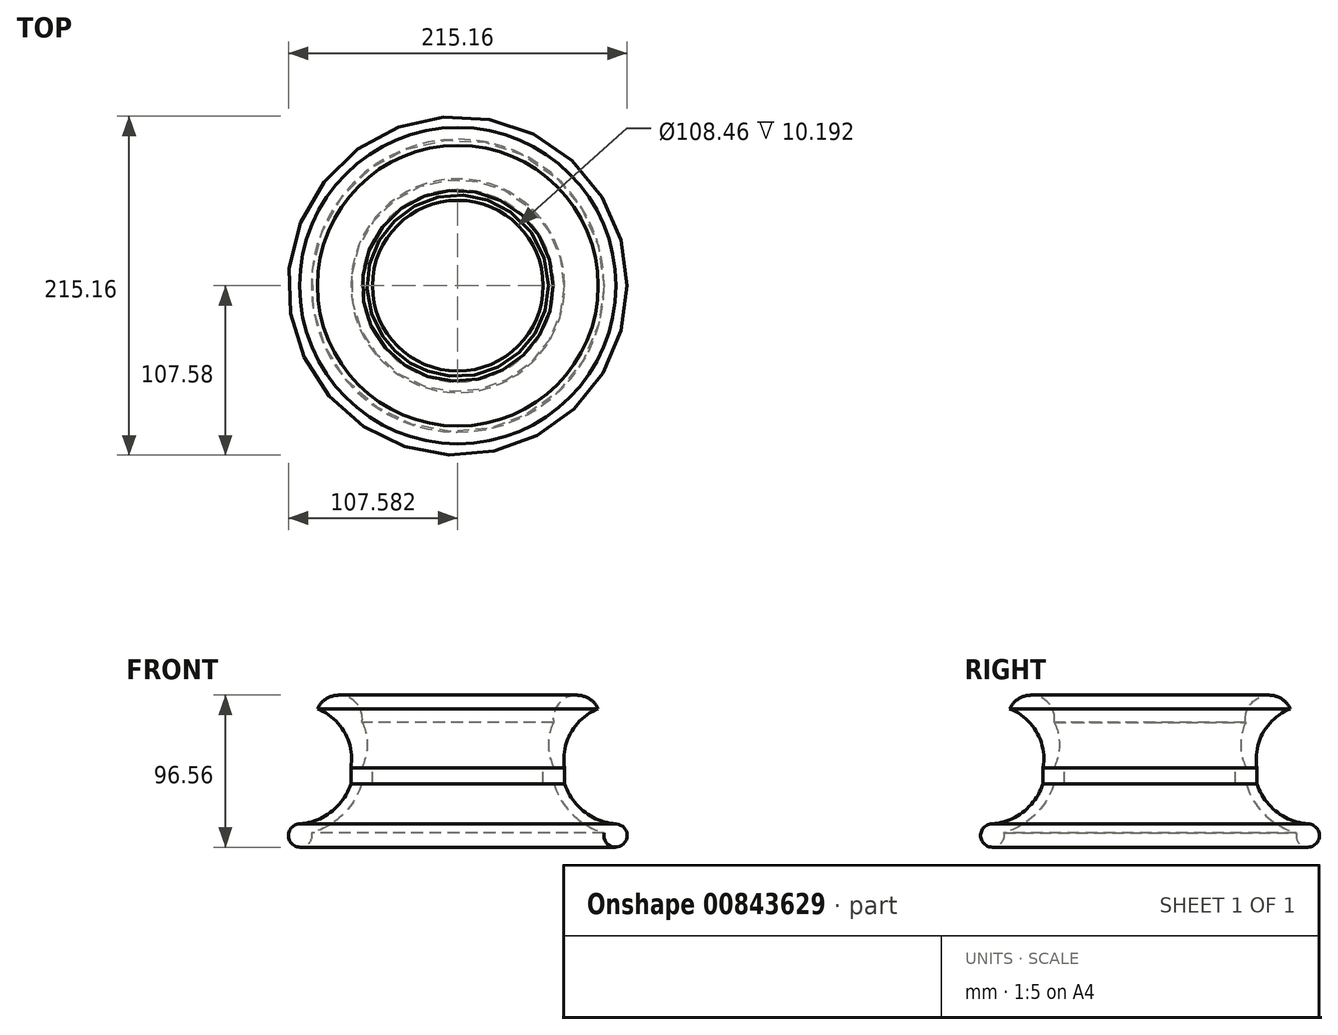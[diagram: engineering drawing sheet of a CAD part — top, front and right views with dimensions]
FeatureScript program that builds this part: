
annotation { "Feature Type Name" : "Feature", "Feature Type Description" : "" }
export const myFeature = defineFeature(function(context is Context, id is Id, definition is map)
    precondition{}
    {
        {
            var Q0;
            Q0=qCreatedBy(makeId("Front.planeOp"),FACE);
            var sketch = newSketch(context, id + "F0", { "sketchPlane" : qUnion([Q0])});
            skArc(sketch, "E0", {"start": v(-19.36, 13.55) * mm, "mid": v(-29.85, 30.08) * mm, "end": v(-47.7, 22.04) * mm});
            skLineSegment(sketch, "E1.bottom", {"start": v(-19.62, -15.38) * mm, "end": v(-12.79, -15.38) * mm});
            skLineSegment(sketch, "E1.top", {"start": v(-19.62, -25.58) * mm, "end": v(-12.79, -25.58) * mm});
            skLineSegment(sketch, "E1.left", {"start": v(-26.44, -15.38) * mm, "end": v(-26.44, -25.58) * mm});
            skLineSegment(sketch, "E1.right", {"start": v(-12.79, -15.38) * mm, "end": v(-12.79, -25.58) * mm});
            skArc(sketch, "E2", {"start": v(-59.02, -51.08) * mm, "mid": v(-63.24, -64.33) * mm, "end": v(-51.55, -56.8) * mm});
            skArc(sketch, "E3", {"start": v(-26.44, -15.38) * mm, "mid": v(-30.45, 7.09) * mm, "end": v(-47.7, 22.04) * mm});
            skArc(sketch, "E4", {"start": v(-59.02, -51.08) * mm, "mid": v(-38.87, -43.26) * mm, "end": v(-26.44, -25.58) * mm});
            skArc(sketch, "E5", {"start": v(-51.55, -56.8) * mm, "mid": v(-31.57, -45.3) * mm, "end": v(-19.62, -25.58) * mm});
            skArc(sketch, "E6", {"start": v(-19.62, -15.38) * mm, "mid": v(-16.13, -0.95) * mm, "end": v(-19.36, 13.55) * mm});
            skLineSegment(sketch, "E7", {"start": v(41.44, 15.96) * mm, "end": v(41.44, -36.54) * mm, "construction": true});
            skSolve(sketch);
        }
        {
            var Q0;
            Q0=makeQuery(id+"F0.imprint","IMPRINT",FACE,{"disambiguationData":[TD([[makeQuery(id+"F0.imprint","IMPRINT",EDGE,{"derivedFrom":sQuery(id+"F0.wireOp",EDGE,"E0")}),1.0]])]});
            var Q1;
            Q1=sQuery(id+"F0.wireOp",EDGE,"E7");
            revolve(context, id + "F1", {"surfaceOperationType" : NewSurfaceOperationType.NEW, "entities" : qUnion([Q0]), "axis" : qUnion([Q1]), "revolveType" : RevolveType.FULL});
        }
    });
